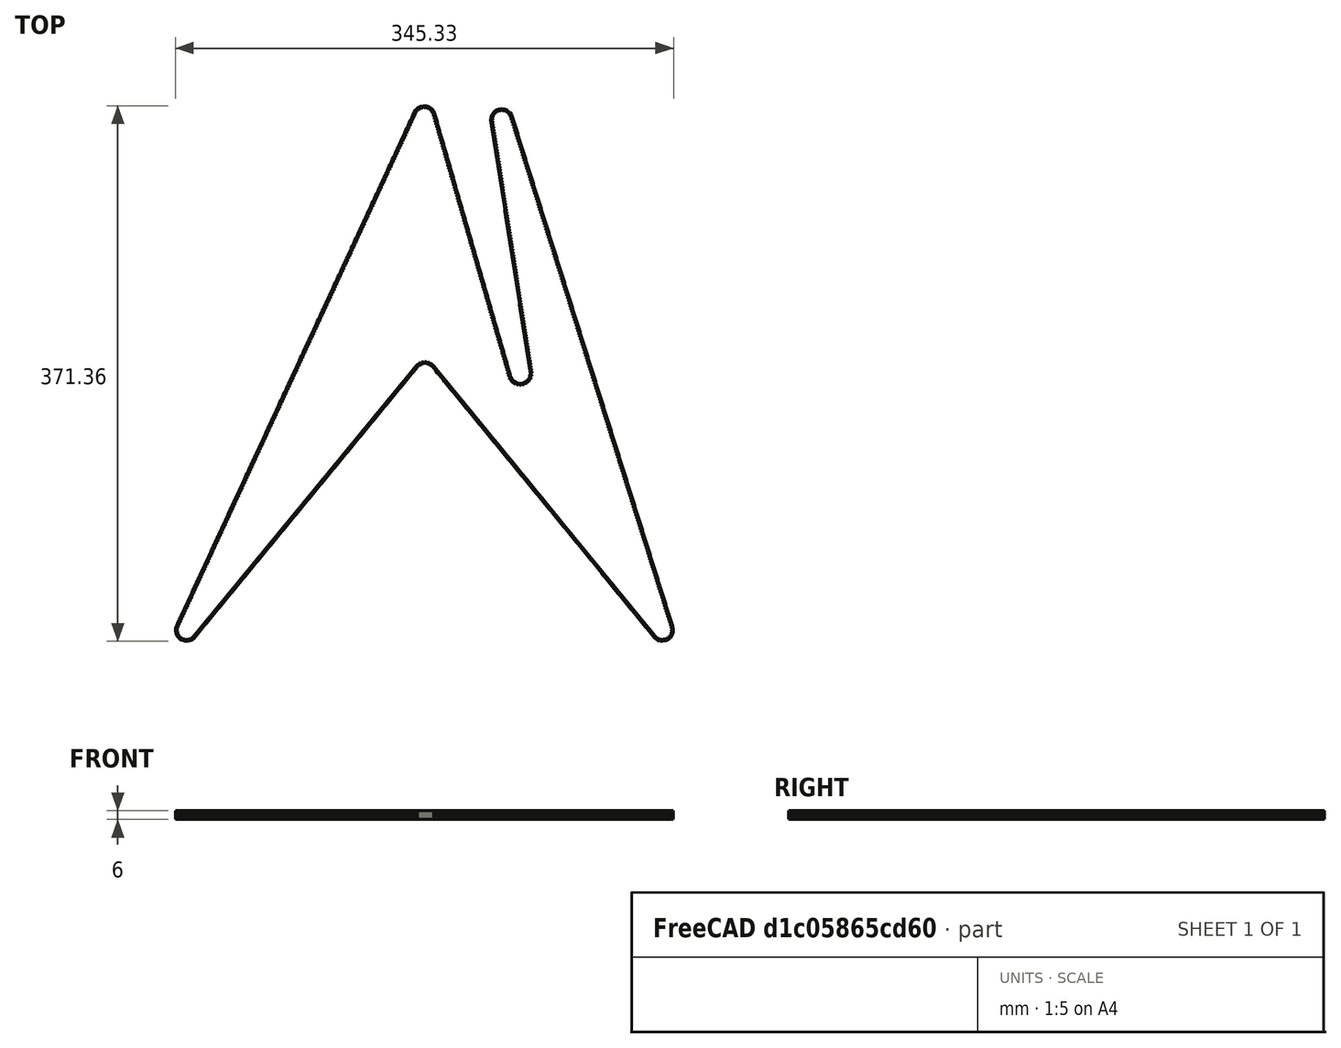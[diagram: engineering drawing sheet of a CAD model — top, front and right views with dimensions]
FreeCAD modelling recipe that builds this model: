
FCSTD DOCUMENT  (FreeCAD 0.16R4945 (Git))
Label: GT2-Belt_Z
License: All rights reserved
LicenseURL: http://en.wikipedia.org/wiki/All_rights_reserved
objects: Part::Part2DObjectPython×17, Sketcher::SketchObject×6, Part::Sweep×4, App::DocumentObjectGroup×3, Part::FeaturePython×2, Part::MultiFuse×2, PartDesign::Pad×1, Part::Compound×1
note: 34 computed .brp shape members not serialized (recipe doc carries the construction recipe); baked Part::Feature solids carry a one-line shape summary decoded from their .brp

FEATURE [Sketcher::SketchObject] Sketch002  label="Timing Belt Master Sketch"
  Placement = pos=(0,0,0) rot=(1,0,0;1.5708rad)
  sketch-geometry (11):
    g0: Circle CenterX=0 CenterY=-0.449 CenterZ=0 NormalX=0 NormalY=0 NormalZ=1 Radius=0.555
    g1: LineSegment [constr] StartX=-1 StartY=-1.004 StartZ=0 EndX=1 EndY=-1.004 EndZ=0
    g2: LineSegment StartX=-1 StartY=-0.254 StartZ=0 EndX=1 EndY=-0.254 EndZ=0
    g3: LineSegment StartX=-1 StartY=0.376 StartZ=0 EndX=1 EndY=0.376 EndZ=0
    g4: LineSegment StartX=-1 StartY=0.376 StartZ=0 EndX=-1 EndY=-1.004 EndZ=0
    g5: LineSegment StartX=1 StartY=0.376 StartZ=0 EndX=1 EndY=-1.004 EndZ=0
    g6: LineSegment [constr] StartX=-1 StartY=-0.449 StartZ=0 EndX=1 EndY=-0.449 EndZ=0
    g7: Circle CenterX=-0.740175 CenterY=-0.404 CenterZ=0 NormalX=0 NormalY=0 NormalZ=1 Radius=0.15
    g8: Circle CenterX=0.740175 CenterY=-0.404 CenterZ=0 NormalX=0 NormalY=0 NormalZ=1 Radius=0.15
    g9: Circle CenterX=-0.4 CenterY=-0.254 CenterZ=0 NormalX=0 NormalY=0 NormalZ=1 Radius=1
    g10: Circle CenterX=0.4 CenterY=-0.254 CenterZ=0 NormalX=0 NormalY=0 NormalZ=1 Radius=1
  constraints (33):
    c: Radius(g0) = 0.555
    c: PointOnObject(g0,g-2)
    c: Horizontal(g1)
    c: Tangent(g1,g0)
    c: DistanceX(g1) = 2
    c: Symmetric(g1,g1,g-2)
    c: Horizontal(g2)
    c: DistanceY(g2,g1) = -0.75
    c: Horizontal(g3)
    c: Equal(g1,g2)
    c: Equal(g2,g3)
    c: Vertical(g4)
    c: Coincident(g4,g1)
    c: Coincident(g4,g3)
    c: PointOnObject(g2,g4)
    c: Coincident(g5,g1)
    c: Coincident(g5,g3)
    c: DistanceY(g3,g1) = -1.38
    c: PointOnObject(g0,g6)
    c: DistanceY(g-1,g2) = -0.254
    c: Horizontal(g6)
    c: PointOnObject(g6,g4)
    c: PointOnObject(g6,g5)
    c: Radius(g7) = 0.15
    c: Equal(g8,g7)
    c: Symmetric(g7,g8,g-2)
    c: Radius(g9) = 1
    c: Equal(g10,g9)
    c: Symmetric(g10,g9,g-2)
    c: DistanceX(g-1,g10) = 0.4
    c: DistanceY(g7,g3) = 0.78
    c: DistanceX(g7,g3) = -0.259825
    c: PointOnObject(g10,g2)
FEATURE [App::DocumentObjectGroup] Group  label="Master Sketch"
  Group = -> [Sketch002]
FEATURE [Part::Part2DObjectPython] Circle  # Draft 2D object (typed FeaturePython)
  FirstAngle = 0
  LastAngle = 0
  MakeFace = true
  Placement = pos=(0,-0.449,0) rot=(0,0,1;0rad)
  Radius = 0.555
FEATURE [Part::Part2DObjectPython] Line  # Draft 2D object (typed FeaturePython)
  ChamferSize = 0
  Closed = false
  End = (1,-0.254,0)
  FilletRadius = 0
  MakeFace = true
  Points = (2) [(-1,-0.254,0),(1,-0.254,0)]
  Start = (-1,-0.254,0)
FEATURE [Part::Part2DObjectPython] DWire  # Draft 2D object (typed FeaturePython)
  ChamferSize = 0
  Closed = false
  End = (1,-1.004,0)
  FilletRadius = 0
  MakeFace = true
  Points = (4) [(-1,-1.004,0),(-1,0.376,0),(1,0.376,0),(1,-1.004,0)]
  Start = (-1,-1.004,0)
FEATURE [Part::Part2DObjectPython] Circle001  # Draft 2D object (typed FeaturePython)
  FirstAngle = 0
  LastAngle = 0
  MakeFace = true
  Placement = pos=(-0.740175,-0.404,0) rot=(0,0,1;0rad)
  Radius = 0.15
FEATURE [Part::Part2DObjectPython] Circle002  # Draft 2D object (typed FeaturePython)
  FirstAngle = 0
  LastAngle = 0
  MakeFace = true
  Placement = pos=(0.740175,-0.404,0) rot=(0,0,1;0rad)
  Radius = 0.15
FEATURE [Part::Part2DObjectPython] Circle003  # Draft 2D object (typed FeaturePython)
  FirstAngle = 0
  LastAngle = 0
  MakeFace = true
  Placement = pos=(-0.4,-0.254,0) rot=(0,0,1;0rad)
  Radius = 1
FEATURE [Part::Part2DObjectPython] Circle004  # Draft 2D object (typed FeaturePython)
  FirstAngle = 0
  LastAngle = 0
  MakeFace = true
  Placement = pos=(0.4,-0.254,0) rot=(0,0,1;0rad)
  Radius = 1
FEATURE [App::DocumentObjectGroup] Group001  label="Draft from Sketch"
  Group = -> [Circle,Line,DWire,Circle001,Circle002,Circle003,Circle004]
FEATURE [Part::Part2DObjectPython] Arc  # Draft 2D object (typed FeaturePython)
  FirstAngle = 7.49472
  LastAngle = 90
  MakeFace = false
  Placement = pos=(-0.740175,-0.404,0) rot=(0,0,1;0rad)
  Radius = 0.15
FEATURE [Part::Part2DObjectPython] Arc001  # Draft 2D object (typed FeaturePython)
  FirstAngle = 90
  LastAngle = 172.505
  MakeFace = false
  Placement = pos=(0.740175,-0.404,0) rot=(0,0,1;0rad)
  Radius = 0.15
FEATURE [Part::Part2DObjectPython] Line001  # Draft 2D object (typed FeaturePython)
  ChamferSize = 0
  Closed = false
  End = (-1,-0.254,0)
  FilletRadius = 0
  MakeFace = false
  Points = (2) [(-0.740175,-0.254,0),(-1,-0.254,0)]
  Start = (-0.740175,-0.254,0)
FEATURE [Part::Part2DObjectPython] Line002  # Draft 2D object (typed FeaturePython)
  ChamferSize = 0
  Closed = false
  End = (1,-0.254,0)
  FilletRadius = 0
  MakeFace = false
  Points = (2) [(0.740175,-0.254,0),(1,-0.254,0)]
  Start = (0.740175,-0.254,0)
FEATURE [Part::Part2DObjectPython] Arc002  # Draft 2D object (typed FeaturePython)
  FirstAngle = -154.011
  LastAngle = -25.9892
  MakeFace = false
  Placement = pos=(0,-0.449,0) rot=(0,0,1;0rad)
  Radius = 0.555
FEATURE [Part::Part2DObjectPython] Arc003  # Draft 2D object (typed FeaturePython)
  FirstAngle = -25.9892
  LastAngle = -7.49472
  MakeFace = false
  Placement = pos=(-0.4,-0.254,0) rot=(0,0,1;0rad)
  Radius = 1
FEATURE [Part::Part2DObjectPython] Arc004  # Draft 2D object (typed FeaturePython)
  FirstAngle = -172.505
  LastAngle = -154.011
  MakeFace = false
  Placement = pos=(0.4,-0.254,0) rot=(0,0,1;0rad)
  Radius = 1
FEATURE [Part::Part2DObjectPython] Line003  # Draft 2D object (typed FeaturePython)
  ChamferSize = 0
  Closed = false
  End = (-1,0.376,0)
  FilletRadius = 0
  MakeFace = false
  Points = (2) [(-1,-0.254,0),(-1,0.376,0)]
  Start = (-1,-0.254,0)
FEATURE [Part::Part2DObjectPython] Line004  # Draft 2D object (typed FeaturePython)
  ChamferSize = 0
  Closed = false
  End = (1,0.376,0)
  FilletRadius = 0
  MakeFace = false
  Points = (2) [(1,-0.254,0),(1,0.376,0)]
  Start = (1,-0.254,0)
FEATURE [Part::Part2DObjectPython] Line005  # Draft 2D object (typed FeaturePython)
  ChamferSize = 0
  Closed = false
  End = (1,0.376,0)
  FilletRadius = 0
  MakeFace = false
  Points = (2) [(-1,0.376,0),(1,0.376,0)]
  Start = (-1,0.376,0)
FEATURE [App::DocumentObjectGroup] Group002  label="Outline from Draft"
  Group = -> [Arc,Arc001,Line001,Line002,Arc002,Arc003,Arc004,Line003,Line004,Line005]
FEATURE [Sketcher::SketchObject] Sketch003  label="Timing Belt sketch from outline"
  Placement = pos=(0,0,0) rot=(0,-0.707107,0.707107;3.14159rad)
  sketch-geometry (10):
    g0: ArcOfCircle CenterX=-0.740173 CenterY=-0.403997 CenterZ=0 NormalX=0 NormalY=0 NormalZ=1 Radius=0.149997 StartAngle=0.134719 EndAngle=1.57082
    g1: LineSegment StartX=1 StartY=-0.254 StartZ=0 EndX=1 EndY=0.376 EndZ=0
    g2: ArcOfCircle CenterX=0.740176 CenterY=-0.404 CenterZ=0 NormalX=0 NormalY=0 NormalZ=1 Radius=0.15 StartAngle=1.5708 EndAngle=3.01411
    g3: LineSegment StartX=0.740176 StartY=-0.254 StartZ=0 EndX=1 EndY=-0.254 EndZ=0
    g4: LineSegment StartX=-0.740176 StartY=-0.254 StartZ=0 EndX=-1 EndY=-0.254 EndZ=0
    g5: ArcOfCircle CenterX=0 CenterY=-0.448894 CenterZ=0 NormalX=0 NormalY=0 NormalZ=1 Radius=0.555048 StartAngle=3.59519 EndAngle=5.83002
    g6: ArcOfCircle CenterX=-0.400001 CenterY=-0.254 CenterZ=0 NormalX=0 NormalY=0 NormalZ=1 Radius=1 StartAngle=5.82992 EndAngle=6.15188
    g7: LineSegment StartX=-1 StartY=0.376 StartZ=0 EndX=1 EndY=0.376 EndZ=0
    g8: ArcOfCircle CenterX=0.400001 CenterY=-0.254 CenterZ=0 NormalX=0 NormalY=0 NormalZ=1 Radius=1 StartAngle=3.27181 EndAngle=3.5951
    g9: LineSegment StartX=-1 StartY=-0.254 StartZ=0 EndX=-1 EndY=0.376 EndZ=0
  constraints (34):
    c: Coincident(g7,g9)
    c: Coincident(g1,g7)
    c: Coincident(g4,g9)
    c: Coincident(g0,g4)
    c: Coincident(g0,g8)
    c: Coincident(g5,g8)
    c: Coincident(g5,g6)
    c: Coincident(g2,g6)
    c: Coincident(g2,g3)
    c: Coincident(g1,g3)
    c: PointOnObject(g5,g-2)
    c: DistanceX(g7) = 2
    c: Symmetric(g7,g1,g-2)
    c: Equal(g9,g1)
    c: Equal(g4,g3)
    c: DistanceY(g9) = 0.63
    c: DistanceX(g4) = -0.259824
    c: Vertical(g9)
    c: Horizontal(g4)
    c: Horizontal(g3)
    c: Symmetric(g1,g4,g-2)
    c: DistanceY(g-1,g7) = 0.376
    c: DistanceX(g8) = 0.400001
    c: DistanceY(g8) = -0.254
    c: DistanceX(g6) = -0.400001
    c: DistanceY(g6) = -0.254
    c: DistanceX(g0) = -0.740173
    c: DistanceY(g0) = -0.403997
    c: DistanceX(g2) = 0.740176
    c: DistanceY(g2) = -0.404
    c: Equal(g8,g6)
    c: Radius(g5) = 0.555048
    c: DistanceX(g5) = 0.499025
    c: DistanceY(g5) = -0.691901
FEATURE [PartDesign::Pad] Pad  label="Timing Belt GT2"
  Length = 6
  Length2 = 100
  Placement = pos=(0,0,0) rot=(0,-0.707107,0.707107;3.14159rad)
  Sketch = -> Sketch003
  Type = 0
FEATURE [Sketcher::SketchObject] Sketch004  label="Belt-Back"
  Placement = pos=(190.157,-169,5.996) rot=(0,0,1;2.708rad)
  sketch-geometry (4):
    g0: LineSegment StartX=0.266 StartY=0 StartZ=0 EndX=0.486 EndY=0 EndZ=0
    g1: LineSegment StartX=0.486 StartY=0 StartZ=0 EndX=0.486 EndY=-6 EndZ=0
    g2: LineSegment StartX=0.486 StartY=-6 StartZ=0 EndX=0.266 EndY=-6 EndZ=0
    g3: LineSegment StartX=0.266 StartY=-6 StartZ=0 EndX=0.266 EndY=0 EndZ=0
  constraints (12):
    c: Coincident(g0,g1)
    c: Coincident(g1,g2)
    c: Coincident(g2,g3)
    c: Coincident(g3,g0)
    c: Horizontal(g0)
    c: Horizontal(g2)
    c: Vertical(g1)
    c: Vertical(g3)
    c: Distance(g1) = 6
    c: Distance(g0) = 0.22
    c: DistanceY(g-1,g0) = 0
    c: DistanceX(g-1,g0) = 0.266
FEATURE [Part::FeaturePython] z_Assmbly_01  label="z_Assembly_01"  # a2plus imported part (geometry in sourceFile) (typed FeaturePython)
  Placement = pos=(0,-395,-81) rot=(0,0,1;0rad)
  fixedPosition = true
  sourceFile = <userpath>/CloudStation/Hobbyprojekte/3D Drucker/CoreXY/Assembly/z-Assmbly.FCStd
  timeLastImport = 1445803847
  updateColors = true
FEATURE [Sketcher::SketchObject] Sketch  label="Beltpath"
  ExternalGeometry = -> [z_Assmbly_01]
  Placement = pos=(0,-395,0.4) rot=(0,0,1;0rad)
  Support = -> z_Assmbly_01 [Face606]
  sketch-geometry (20):
    g0: LineSegment [constr] StartX=83.8508 StartY=26.7539 StartZ=0 EndX=84.2903 EndY=26.523 EndZ=0
    g1: LineSegment [constr] StartX=86.9467 StartY=32.1125 StartZ=0 EndX=84.0705 EndY=26.6385 EndZ=0
    g2: ArcOfCircle CenterX=220.35 CenterY=220.05 CenterZ=0 NormalX=0 NormalY=0 NormalZ=1 Radius=7.25 StartAngle=0.68649 EndAngle=2.45279
    g3: ArcOfCircle CenterX=286.35 CenterY=220.05 CenterZ=0 NormalX=0 NormalY=0 NormalZ=1 Radius=7.25 StartAngle=3.42297 EndAngle=6.43798
    g4: ArcOfCircle CenterX=219.82 CenterY=398 CenterZ=0 NormalX=0 NormalY=0 NormalZ=1 Radius=7.25 StartAngle=0.28138 EndAngle=2.708
    g5: ArcOfCircle CenterX=55 CenterY=42 CenterZ=0 NormalX=0 NormalY=0 NormalZ=1 Radius=7.25 StartAngle=2.708 EndAngle=5.52273
    g6: LineSegment StartX=60.2528 StartY=37.0029 StartZ=0 EndX=214.753 EndY=224.658 EndZ=0
    g7: LineSegment StartX=225.958 StartY=224.645 StartZ=0 EndX=379.392 EndY=37.4048 EndZ=0
    g8: ArcOfCircle CenterX=385 CenterY=42 CenterZ=0 NormalX=0 NormalY=0 NormalZ=1 Radius=7.25 StartAngle=3.82808 EndAngle=6.58814
    g9: LineSegment StartX=391.915 StartY=44.1768 StartZ=0 EndX=280.486 EndY=398.177 EndZ=0
    g10: ArcOfCircle CenterX=273.57 CenterY=396 CenterZ=0 NormalX=0 NormalY=0 NormalZ=1 Radius=7.25 StartAngle=0.304955 EndAngle=3.29639
    g11: LineSegment StartX=266.407 StartY=394.882 StartZ=0 EndX=293.513 EndY=221.168 EndZ=0
    g12: Circle [constr] CenterX=220.35 CenterY=220.05 CenterZ=0 NormalX=0 NormalY=0 NormalZ=1 Radius=7.25
    g13: Circle [constr] CenterX=286.35 CenterY=220.05 CenterZ=0 NormalX=0 NormalY=0 NormalZ=1 Radius=7.25
    g14: Circle [constr] CenterX=55 CenterY=42 CenterZ=0 NormalX=0 NormalY=0 NormalZ=1 Radius=7.25
    g15: Circle [constr] CenterX=219.82 CenterY=398 CenterZ=0 NormalX=0 NormalY=0 NormalZ=1 Radius=7.25
    g16: Circle [constr] CenterX=385 CenterY=42 CenterZ=0 NormalX=0 NormalY=0 NormalZ=1 Radius=7.25
    g17: Circle [constr] CenterX=273.57 CenterY=396 CenterZ=0 NormalX=0 NormalY=0 NormalZ=1 Radius=7.25
    g18: LineSegment StartX=279.385 StartY=218.037 StartZ=0 EndX=226.785 EndY=400.013 EndZ=0
    g19: LineSegment StartX=213.241 StartY=401.046 StartZ=0 EndX=48.4209 EndY=45.046 EndZ=0
  constraints (48):
    c: Perpendicular(g0,g1)
    c: Tangent(g7,g8) = -1.5708
    c: Coincident(g8,g9)
    c: Tangent(g9,g10) = -1.5708
    c: PointOnObject(g1,g0)
    c: Symmetric(g0,g0,g1)
    c: Tangent(g8,g9) = -1.5708
    c: Radius(g12) = 7.25
    c: Coincident(g2,g12)
    c: Coincident(g13,g3)
    c: Coincident(g14,g5)
    c: Coincident(g15,g4)
    c: PointOnObject(g3,g13)
    c: Coincident(g16,g8)
    c: PointOnObject(g7,g16)
    c: PointOnObject(g9,g17)
    c: Coincident(g10,g17)
    c: Equal(g14,g12)
    c: Equal(g12,g16)
    c: Equal(g16,g13)
    c: Equal(g13,g15)
    c: Equal(g15,g17)
    c: PointOnObject(g4,g15)
    c: PointOnObject(g2,g12)
    c: PointOnObject(g5,g14)
    c: Coincident(g2,g6)
    c: Tangent(g12,g6)
    c: Coincident(g7,g2)
    c: Tangent(g2,g7)
    c: Coincident(g18,g3)
    c: Coincident(g18,g4)
    c: Tangent(g3,g18)
    c: Tangent(g4,g18)
    c: Coincident(g19,g4)
    c: Tangent(g19,g5)
    c: Tangent(g19,g4)
    c: Coincident(g4,g-3)
    c: Coincident(g5,g-4)
    c: Coincident(g8,g-5)
    c: Coincident(g2,g-6)
    c: Coincident(g11,g3)
    c: Tangent(g3,g11)
    c: Coincident(g3,g-7)
    c: Coincident(g10,g11)
    c: Tangent(g10,g11)
    c: Coincident(g10,g-8)
    c: Coincident(g6,g5)
    c: Coincident(g5,g19)
FEATURE [Sketcher::SketchObject] Sketch005  label="Simple Belt"
  Placement = pos=(0,-327.765,0) rot=(0.954754,-0.210292,-0.210292;1.61708rad)
  sketch-geometry (4):
    g0: LineSegment StartX=52.5058 StartY=0.441907 StartZ=0 EndX=54.0058 EndY=0.441907 EndZ=0
    g1: LineSegment StartX=54.0058 StartY=0.441907 StartZ=0 EndX=54.0058 EndY=6.44191 EndZ=0
    g2: LineSegment StartX=54.0058 StartY=6.44191 StartZ=0 EndX=52.5058 EndY=6.44191 EndZ=0
    g3: LineSegment StartX=52.5058 StartY=6.44191 StartZ=0 EndX=52.5058 EndY=0.441907 EndZ=0
  constraints (10):
    c: Coincident(g0,g1)
    c: Coincident(g1,g2)
    c: Coincident(g2,g3)
    c: Coincident(g3,g0)
    c: Horizontal(g0)
    c: Horizontal(g2)
    c: Vertical(g1)
    c: Vertical(g3)
    c: Distance(g0) = 1.5
    c: Distance(g3) = 6
FEATURE [Part::Sweep] Sweep
  Frenet = false
  Sections = -> [Sketch005]
  Solid = true
  Spine = -> Sketch [Edge4,Edge5,Edge6,Edge7,Edge8,Edge9,Edge10,Edge11,Edge12,Edge1]
  Transition = 1
FEATURE [Part::Sweep] Sweep001
  Frenet = false
  Sections = -> [Sketch005]
  Solid = true
  Spine = -> Sketch [Edge3,Edge2]
  Transition = 1
FEATURE [Part::MultiFuse] Fusion  label="Belt_simple"
  Shapes = -> [Sweep001,Sweep]
FEATURE [Sketcher::SketchObject] Sketch006  label="Belt Array Back"
  Placement = pos=(0,-327.765,0) rot=(0.954754,-0.210292,-0.210292;1.61708rad)
  sketch-geometry (4):
    g0: LineSegment StartX=52.7753 StartY=0.4 StartZ=0 EndX=52.9953 EndY=0.4 EndZ=0
    g1: LineSegment StartX=52.9953 StartY=0.4 StartZ=0 EndX=52.9953 EndY=-5.6 EndZ=0
    g2: LineSegment StartX=52.9953 StartY=-5.6 StartZ=0 EndX=52.7753 EndY=-5.6 EndZ=0
    g3: LineSegment StartX=52.7753 StartY=-5.6 StartZ=0 EndX=52.7753 EndY=0.4 EndZ=0
  constraints (11):
    c: Coincident(g0,g1)
    c: Coincident(g1,g2)
    c: Coincident(g2,g3)
    c: Coincident(g3,g0)
    c: Horizontal(g0)
    c: Horizontal(g2)
    c: Vertical(g1)
    c: Vertical(g3)
    c: Distance(g0) = 0.22
    c: DistanceY(g-1,g0) = 0.4
    c: Distance(g3) = 6
FEATURE [Part::FeaturePython] PathArray  # WARN: FeaturePython — macro-defined, semantics opaque (R4)
  Align = true
  Base = -> Pad
  Count = 865
  PathObj = -> Sketch
  Xlate = (0,0,0)
FEATURE [Part::Sweep] Sweep002
  Frenet = false
  Sections = -> [Sketch006]
  Solid = true
  Spine = -> Sketch [Edge4,Edge5,Edge6,Edge7,Edge8,Edge9,Edge10,Edge11,Edge12,Edge1]
  Transition = 1
FEATURE [Part::Sweep] Sweep003
  Frenet = false
  Sections = -> [Sketch006]
  Solid = true
  Spine = -> Sketch [Edge3,Edge2]
  Transition = 1
FEATURE [Part::MultiFuse] Fusion001
  Shapes = -> [Sweep003,Sweep002]
FEATURE [Part::Compound] Compound
  Links = -> [PathArray,Fusion001]
